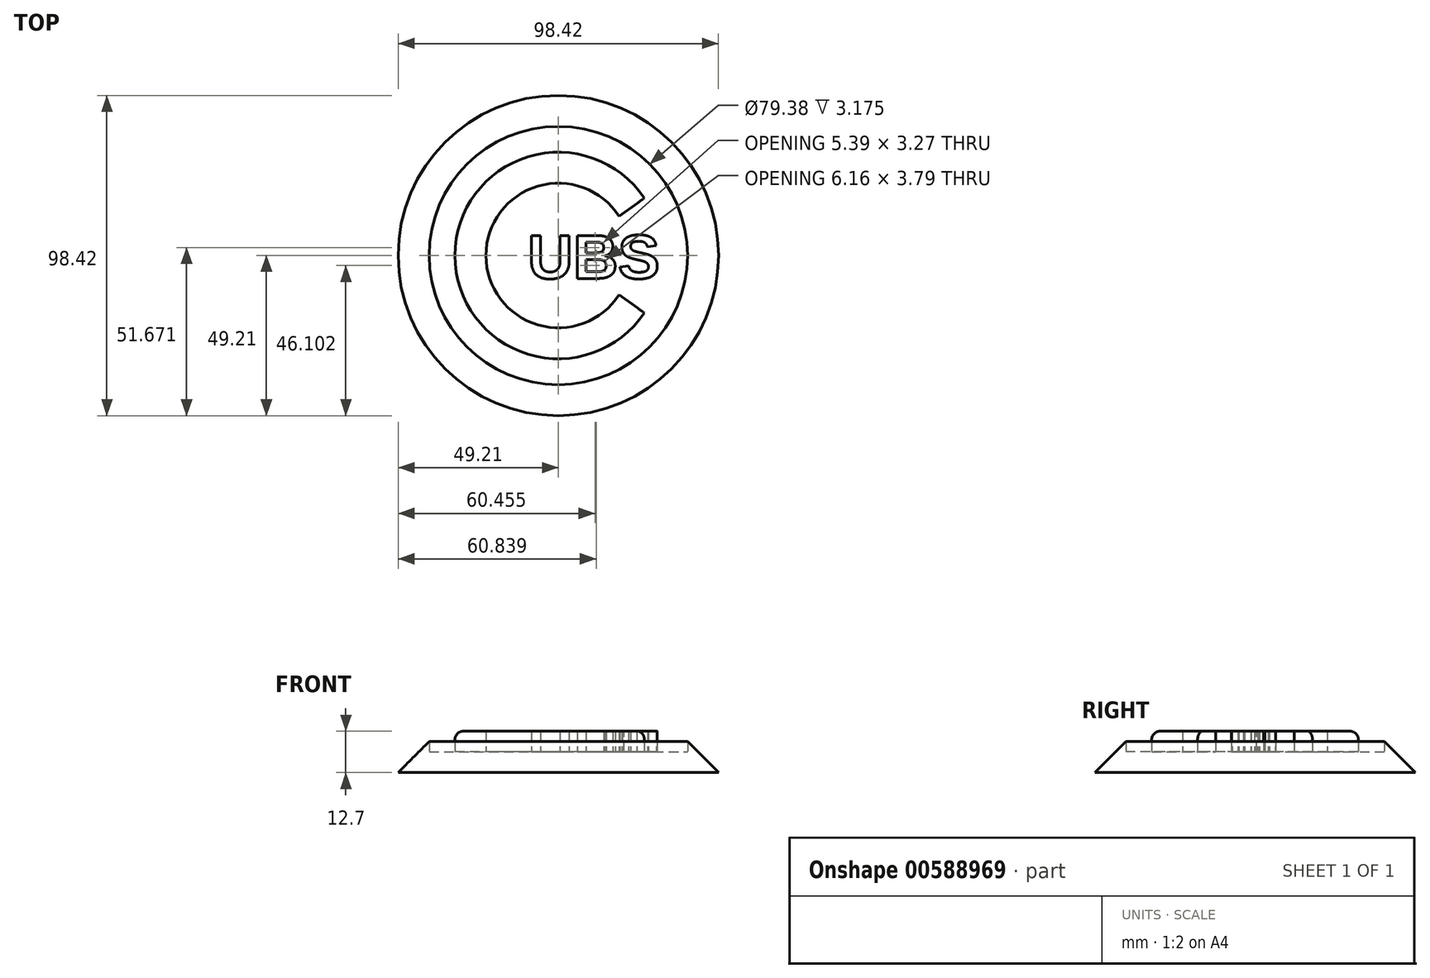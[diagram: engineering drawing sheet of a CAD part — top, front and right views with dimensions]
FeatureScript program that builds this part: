
annotation { "Feature Type Name" : "Feature", "Feature Type Description" : "" }
export const myFeature = defineFeature(function(context is Context, id is Id, definition is map)
    precondition{}
    {
        {
            var Q0;
            Q0=qCreatedBy(makeId("Top.planeOp"),FACE);
            var sketch = newSketch(context, id + "F0", { "sketchPlane" : qUnion([Q0])});
            skCircle(sketch, "E0", {"center": v(0, 0) * mm, "radius": 39.69 * mm});
            skSolve(sketch);
        }
        {
            var Q0;
            Q0=qCreatedBy(makeId("Top.planeOp"),FACE);
            var sketch = newSketch(context, id + "F1", { "sketchPlane" : qUnion([Q0])});
            skArc(sketch, "E1", {"start": v(26.4, 17.64) * mm, "mid": v(-31.75, 0) * mm, "end": v(26.4, -17.64) * mm});
            skArc(sketch, "E2", {"start": v(18.7, 12.03) * mm, "mid": v(-22.23, 0) * mm, "end": v(18.7, -12.03) * mm});
            skLineSegment(sketch, "E3", {"start": v(18.7, 12.03) * mm, "end": v(26.4, 17.64) * mm});
            skLineSegment(sketch, "E4", {"start": v(26.4, 17.64) * mm, "end": v(18.7, 12.03) * mm});
            skLineSegment(sketch, "E5.MirrorCS", {"start": v(26.4, -17.64) * mm, "end": v(18.7, -12.03) * mm});
            skText(sketch, "E6", { "text": "UBS", "fontName": "Arimo-Bold.ttf"});
            const initialGuessF1  = {"E6": [-0.00935, -0.00705, 1, 0, 0.01381]};
            skSetInitialGuess(sketch, initialGuessF1);
            skSolve(sketch);
        }
        {
            var Q0;
            Q0 = qSketchRegion(id + "F1", true);
            extrude(context, id + "F2", {"entities" : qUnion([Q0]), "depth" : 6.35 * mm, "offsetDistance" : 25.4 * mm});
        }
        {
            var Q0;
            Q0=makeQuery(id+"F0.imprint","IMPRINT",FACE,{"disambiguationData":[TD([[makeQuery(id+"F0.imprint","IMPRINT",EDGE,{"derivedFrom":sQuery(id+"F0.wireOp",EDGE,"E0")}),1.0]])]});
            extrude(context, id + "F3", {"entities" : qUnion([Q0]), "oppositeDirection" : true, "depth" : 6.35 * mm, "offsetDistance" : 25.4 * mm});
        }
        {
            var Q0;
            Q0=makeQuery(id+"F3.opExtrude","CAP_FACE",FACE,{"disambiguationData":[OSD([sQuery(id+"F0.wireOp",EDGE,"E0")])],"isStart":false});
            var sketch = newSketch(context, id + "F4", { "sketchPlane" : qUnion([Q0])});
            skCircle(sketch, "E7", {"center": v(0, 0) * mm, "radius": 49.21 * mm});
            skSolve(sketch);
        }
        {
            var Q0;
            Q0=makeQuery(id+"F4.imprint","IMPRINT",FACE,{"disambiguationData":[TD([[makeQuery(id+"F4.imprint","IMPRINT",EDGE,{"derivedFrom":sQuery(id+"F4.wireOp",EDGE,"E7")}),1.0]])]});
            extrude(context, id + "F5", {"entities" : qUnion([Q0]), "operationType" : NewBodyOperationType.ADD, "oppositeDirection" : true, "depth" : 12.7 * mm, "offsetDistance" : 25.4 * mm});
        }
        {
            var Q0;
            Q0=makeQuery(id+"F5.opExtrude","CAP_EDGE",EDGE,{"disambiguationData":[OSD([sQuery(id+"F4.wireOp",EDGE,"E7")])],"isStart":false});
            chamfer(context, id + "F6", {"entities" : qUnion([Q0]), "width" : 12.7 * mm, "tangentPropagation" : true});
        }
        {
            var Q0;
            Q0=makeQuery(id+"F2.opExtrude","CAP_EDGE",EDGE,{"disambiguationData":[OSD([sQuery(id+"F1.wireOp",EDGE,"E1")])],"isStart":false});
            fillet(context, id + "F7", {"entities" : qUnion([Q0]), "radius" : 2.54 * mm, "tangentPropagation" : true, "allowEdgeOverflow" : false});
        }
    });
